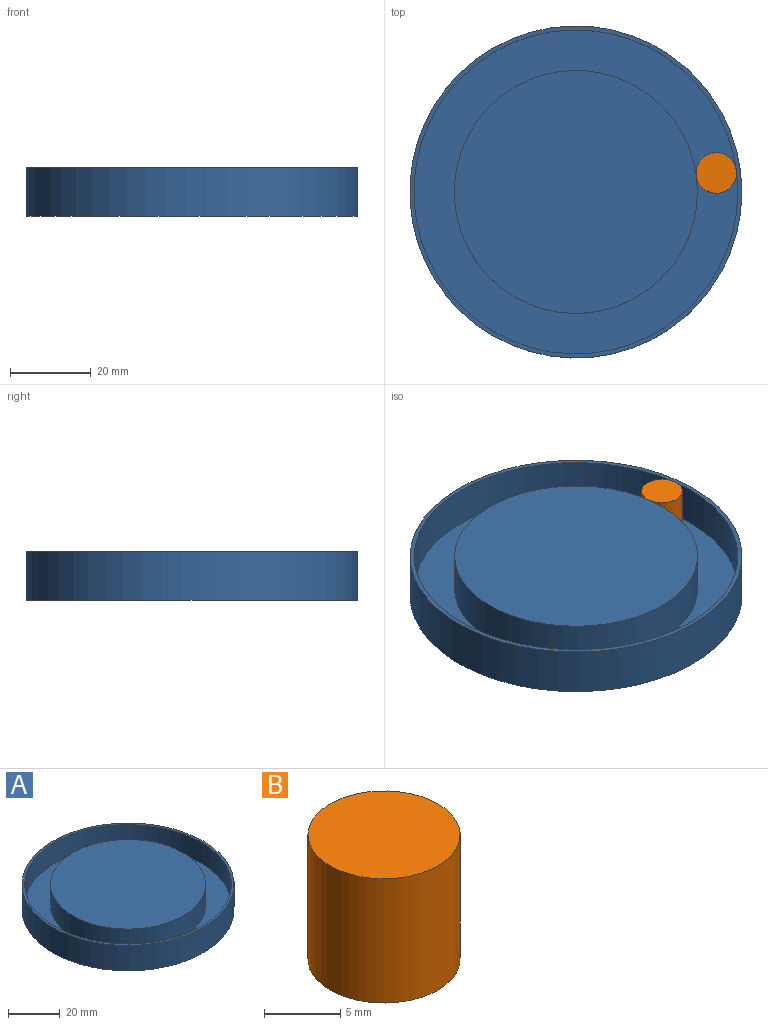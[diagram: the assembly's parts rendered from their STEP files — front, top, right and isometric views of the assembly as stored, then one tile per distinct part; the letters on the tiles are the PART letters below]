
ASSEMBLY  parts=2 mates=1
PART A: 7 faces, bbox 82x82x12 mm
  f0: plane 80x80mm, normal (0,0,1), area 2199.1mm2, adj f1,f3
  f1: cylinder r=30mm len=60mm, axis (0,0,-1), area 1885mm2, adj f0,f2
  f2: plane 60x60mm, normal (0,0,1), area 2827.4mm2, adj f1
  f3: cylinder r=40mm len=80mm, axis (0,0,-1), area 2513.3mm2, adj f0,f4
  f4: plane 82x82mm, normal (0,0,1), area 254.5mm2, adj f3,f6
  f5: plane 82x82mm, normal (0,0,-1), area 5281mm2, adj f6
  f6: cylinder r=41mm len=82mm, axis (0,0,-1), area 3091.3mm2, adj f4,f5
PART B: 3 faces, bbox 10x10x10 mm
  f0: cylinder r=5mm len=10mm, axis (0,0,-1), area 314.2mm2, adj f1,f2
  f1: plane 10x10mm, normal (0,0,1), area 78.5mm2, adj f0
  f2: plane 10x10mm, normal (0,0,-1), area 78.5mm2, adj f0
PLACE A at identity fixed
PLACE B rot(axis=(0,0,1),52.3deg) t=(7,26.1,0)mm
MATE planar B.f0 <-> A.f1  axis (0,0,1) through (34.68,4.69,12)mm
